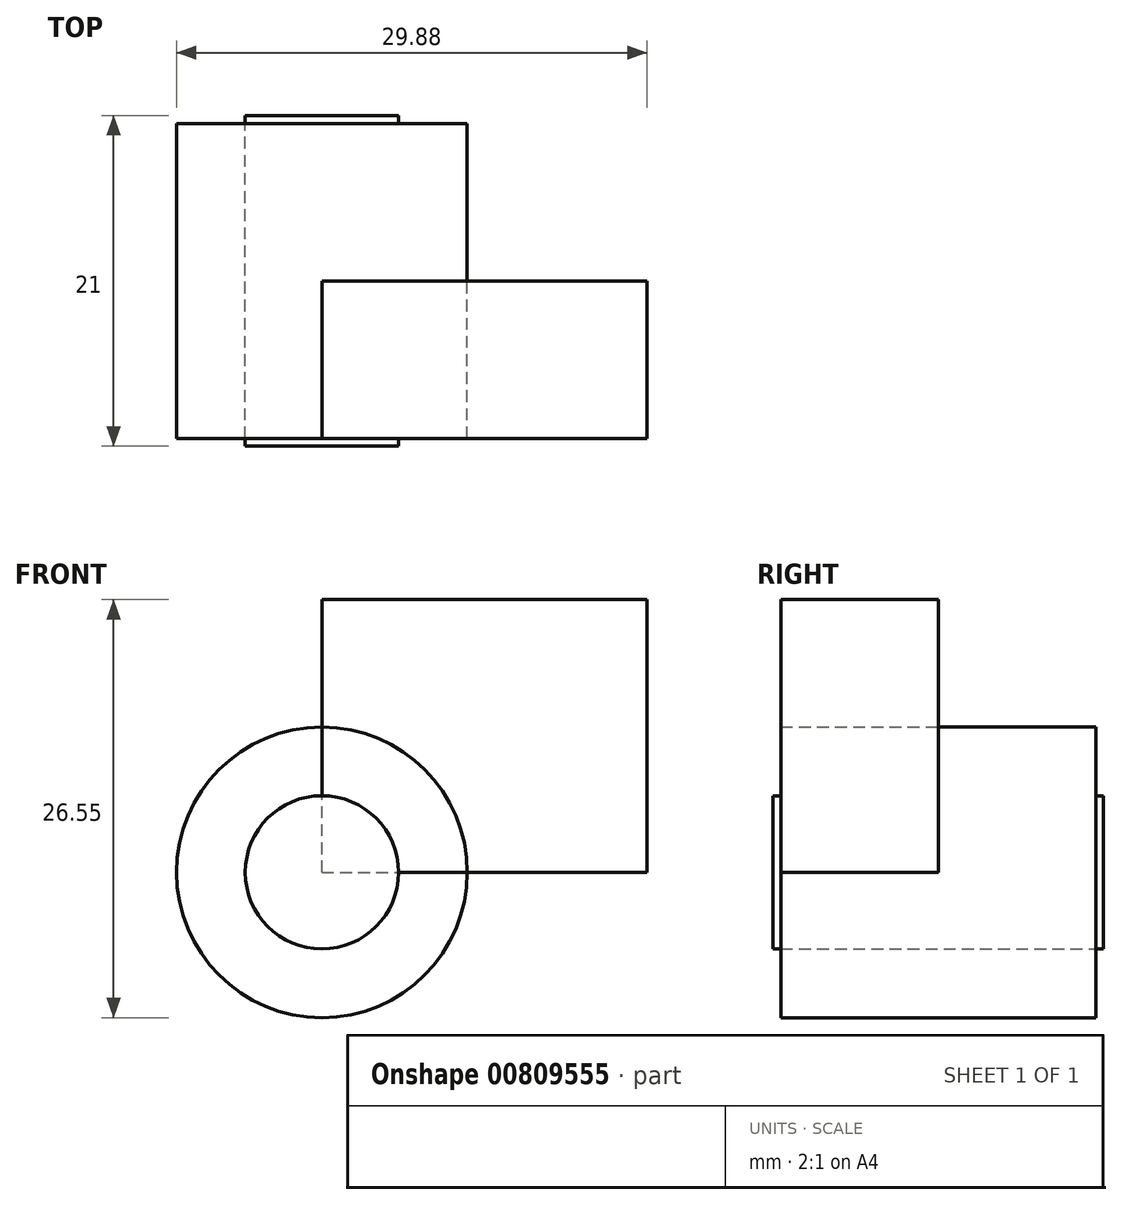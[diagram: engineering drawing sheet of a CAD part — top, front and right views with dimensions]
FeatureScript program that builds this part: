
annotation { "Feature Type Name" : "Feature", "Feature Type Description" : "" }
export const myFeature = defineFeature(function(context is Context, id is Id, definition is map)
    precondition{}
    {
        {
            var Q0;
            Q0=qCreatedBy(makeId("Front.planeOp"),FACE);
            var sketch = newSketch(context, id + "F0", { "sketchPlane" : qUnion([Q0])});
            skCircle(sketch, "E0", {"center": v(0, 0) * mm, "radius": 9.23 * mm});
            skSolve(sketch);
        }
        {
            var Q0;
            Q0=makeQuery(id+"F0.imprint","IMPRINT",FACE,{"disambiguationData":[TD([[makeQuery(id+"F0.imprint","IMPRINT",EDGE,{"derivedFrom":sQuery(id+"F0.wireOp",EDGE,"E0")}),1.0]])]});
            extrude(context, id + "F1", {"entities" : qUnion([Q0]), "endBound" : BoundingType.SYMMETRIC, "depth" : 20 * mm, "offsetDistance" : 25.4 * mm});
        }
        {
            var Q0;
            Q0=qCreatedBy(makeId("Front.planeOp"),FACE);
            var sketch = newSketch(context, id + "F2", { "sketchPlane" : qUnion([Q0])});
            skCircle(sketch, "E1", {"center": v(0, 0) * mm, "radius": 4.87 * mm});
            skSolve(sketch);
        }
        {
            var Q0;
            Q0 = qSketchRegion(id + "F2", true);
            extrude(context, id + "F3", {"entities" : qUnion([Q0]), "endBound" : BoundingType.SYMMETRIC, "depth" : 21 * mm, "offsetDistance" : 25.4 * mm});
        }
        {
            var Q0;
            Q0=qCreatedBy(makeId("Front.planeOp"),FACE);
            var sketch = newSketch(context, id + "F4", { "sketchPlane" : qUnion([Q0])});
            skLineSegment(sketch, "E2.bottom", {"start": v(0, 0) * mm, "end": v(20.65, 0) * mm});
            skLineSegment(sketch, "E2.top", {"start": v(0, 17.32) * mm, "end": v(20.65, 17.32) * mm});
            skLineSegment(sketch, "E2.left", {"start": v(0, 0) * mm, "end": v(0, 17.32) * mm});
            skLineSegment(sketch, "E2.right", {"start": v(20.65, 0) * mm, "end": v(20.65, 17.32) * mm});
            skSolve(sketch);
        }
        {
            var Q0;
            Q0=makeQuery(id+"F4.imprint","IMPRINT",FACE,{"disambiguationData":[TD([[makeQuery(id+"F4.imprint","IMPRINT",EDGE,{"derivedFrom":sQuery(id+"F4.wireOp",EDGE,"E2.bottom")}),1.0]])]});
            extrude(context, id + "F5", {"entities" : qUnion([Q0]), "depth" : 10 * mm, "offsetDistance" : 25.4 * mm});
        }
        {
            var Q0;
            Q0=qCreatedBy(makeId("Origin.pointOp"),VERTEX);
            var Q1;
            Q1=makeQuery(id+"F5.opExtrude","CAP_VERTEX",VERTEX,{"disambiguationData":[OSD([sQuery(id+"F4.wireOp",EDGE,"E2.top"),sQuery(id+"F4.wireOp",EDGE,"E2.right")])],"isStart":false});
            var Q2;
            Q2=makeQuery(id+"F5.opExtrude","CAP_VERTEX",VERTEX,{"disambiguationData":[OSD([sQuery(id+"F4.wireOp",EDGE,"E2.bottom"),sQuery(id+"F4.wireOp",EDGE,"E2.right")])],"isStart":false});
            cPlane(context, id + "F6", {"entities" : qUnion([Q0, Q1, Q2]), "cplaneType" : CPlaneType.THREE_POINT, "offset" : 25.4 * mm, "width" : 152.4 * mm, "height" : 152.4 * mm});
        }
    });
